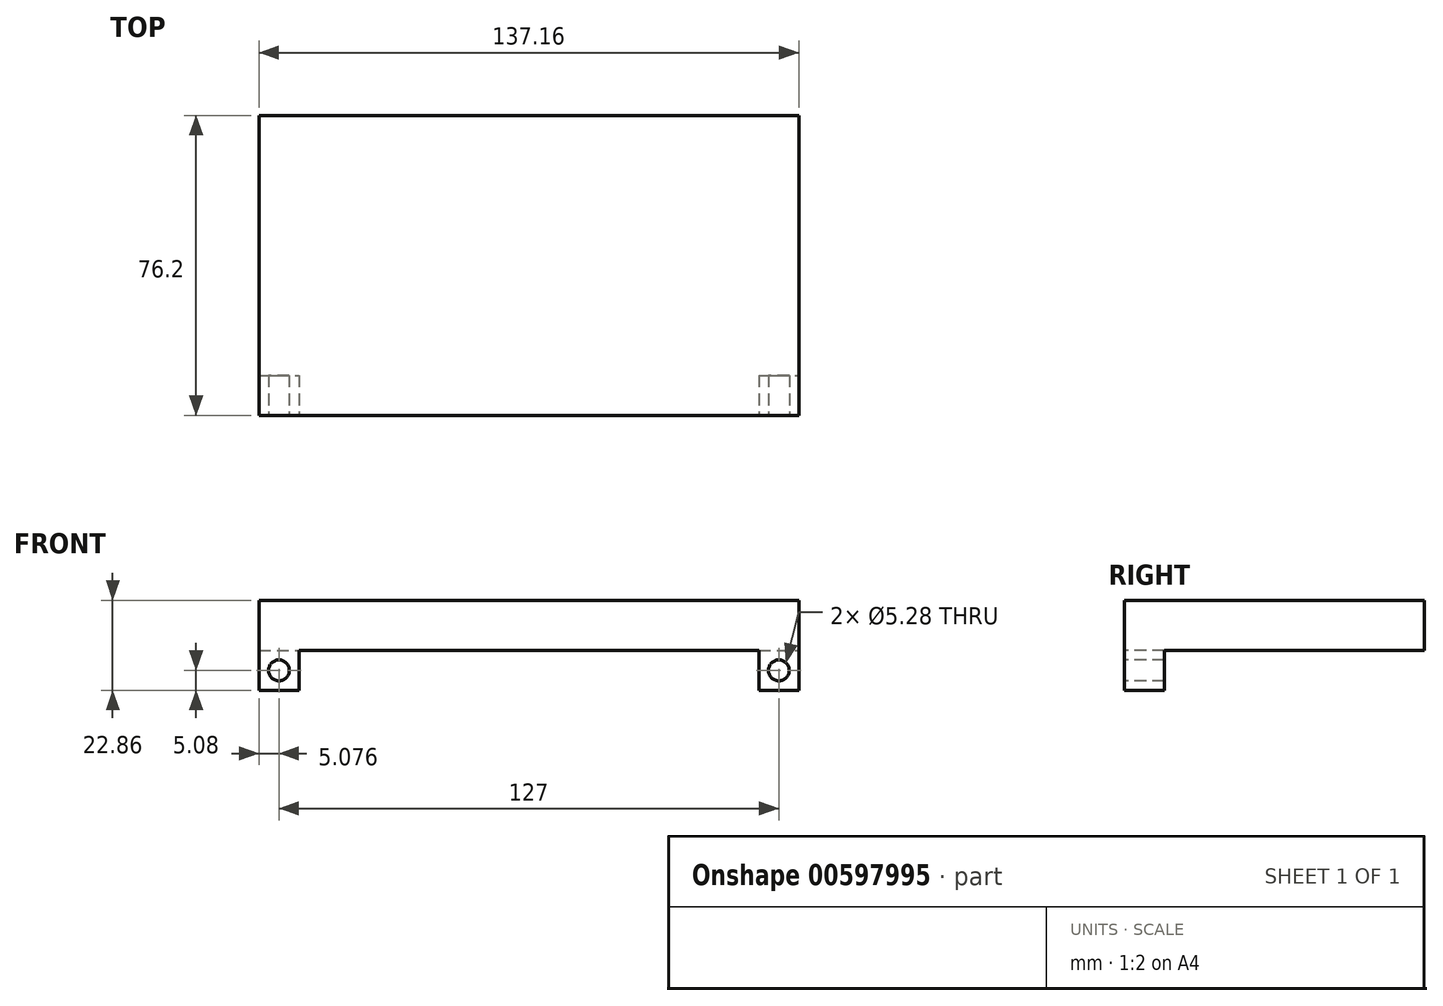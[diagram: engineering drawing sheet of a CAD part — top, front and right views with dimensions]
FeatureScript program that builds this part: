
annotation { "Feature Type Name" : "Feature", "Feature Type Description" : "" }
export const myFeature = defineFeature(function(context is Context, id is Id, definition is map)
    precondition{}
    {
        {
            var Q0;
            Q0=qCreatedBy(makeId("Front.planeOp"),FACE);
            var sketch = newSketch(context, id + "F0", { "sketchPlane" : qUnion([Q0])});
            skLineSegment(sketch, "E0.bottom", {"start": v(-68.27, 6.35) * mm, "end": v(68.89, 6.35) * mm});
            skLineSegment(sketch, "E0.top", {"start": v(-68.27, -6.35) * mm, "end": v(68.89, -6.35) * mm});
            skLineSegment(sketch, "E0.left", {"start": v(-68.27, 6.35) * mm, "end": v(-68.27, -6.35) * mm});
            skLineSegment(sketch, "E0.right", {"start": v(68.89, 6.35) * mm, "end": v(68.89, -6.35) * mm});
            skPoint(sketch, "E0.middle", {"position": v(0.3, 0) * mm});
            skSolve(sketch);
        }
        {
            var Q0;
            Q0=qSketchRegion(id+"F0",true);
            extrude(context, id + "F1", {"entities" : qUnion([Q0]), "depth" : 76.2 * mm, "offsetDistance" : 25.4 * mm});
        }
        {
            var Q0;
            Q0=makeQuery(id+"F1.opExtrude","CAP_FACE",FACE,{"disambiguationData":[OSD([sQuery(id+"F0.wireOp",EDGE,"E0.bottom"),sQuery(id+"F0.wireOp",EDGE,"E0.top"),sQuery(id+"F0.wireOp",EDGE,"E0.left"),sQuery(id+"F0.wireOp",EDGE,"E0.right")])],"isStart":false});
            var sketch = newSketch(context, id + "F2", { "sketchPlane" : qUnion([Q0])});
            skLineSegment(sketch, "E1", {"start": v(-68.27, -6.35) * mm, "end": v(-68.27, -16.5) * mm});
            skLineSegment(sketch, "E2", {"start": v(-68.27, -16.5) * mm, "end": v(-58.11, -16.5) * mm});
            skLineSegment(sketch, "E3", {"start": v(-58.11, -16.5) * mm, "end": v(-58.11, -6.35) * mm});
            skLineSegment(sketch, "E4", {"start": v(-58.11, -6.35) * mm, "end": v(-68.27, -6.35) * mm});
            skLineSegment(sketch, "E5.bottom", {"start": v(68.89, -6.35) * mm, "end": v(58.73, -6.35) * mm});
            skLineSegment(sketch, "E5.top", {"start": v(68.89, -16.51) * mm, "end": v(58.73, -16.51) * mm});
            skLineSegment(sketch, "E5.left", {"start": v(68.89, -6.35) * mm, "end": v(68.89, -16.51) * mm});
            skLineSegment(sketch, "E5.right", {"start": v(58.73, -6.35) * mm, "end": v(58.73, -16.51) * mm});
            skSolve(sketch);
        }
        {
            var Q0;
            Q0=qSketchRegion(id+"F2",true);
            extrude(context, id + "F3", {"entities" : qUnion([Q0]), "operationType" : NewBodyOperationType.ADD, "depth" : -10.16 * mm, "offsetDistance" : 25.4 * mm});
        }
        {
            var Q0;
            Q0=makeQuery(id+"F3.boolean.opBoolean","MERGE",FACE,{"derivedFrom":[makeQuery(id+"F1.opExtrude","CAP_FACE",FACE,{"disambiguationData":[OSD([sQuery(id+"F0.wireOp",EDGE,"E0.bottom"),sQuery(id+"F0.wireOp",EDGE,"E0.top"),sQuery(id+"F0.wireOp",EDGE,"E0.left"),sQuery(id+"F0.wireOp",EDGE,"E0.right")])],"isStart":false}),makeQuery(id+"F3.opExtrude","CAP_FACE",FACE,{"disambiguationData":[OSD([sQuery(id+"F2.wireOp",EDGE,"E1"),sQuery(id+"F2.wireOp",EDGE,"E2"),sQuery(id+"F2.wireOp",EDGE,"E3"),sQuery(id+"F2.wireOp",EDGE,"E4")])],"isStart":true}),makeQuery(id+"F3.opExtrude","CAP_FACE",FACE,{"disambiguationData":[OSD([sQuery(id+"F2.wireOp",EDGE,"E5.bottom"),sQuery(id+"F2.wireOp",EDGE,"E5.top"),sQuery(id+"F2.wireOp",EDGE,"E5.left"),sQuery(id+"F2.wireOp",EDGE,"E5.right")])],"isStart":true})]});
            var sketch = newSketch(context, id + "F4", { "sketchPlane" : qUnion([Q0])});
            skCircle(sketch, "E6", {"center": v(-63.2, -11.43) * mm, "radius": 2.64 * mm});
            skCircle(sketch, "E7", {"center": v(63.8, -11.43) * mm, "radius": 2.64 * mm});
            skSolve(sketch);
        }
        {
            var Q0;
            Q0=qSketchRegion(id+"F4",true);
            extrude(context, id + "F5", {"entities" : qUnion([Q0]), "operationType" : NewBodyOperationType.REMOVE, "oppositeDirection" : true, "depth" : 25.4 * mm, "offsetDistance" : 25.4 * mm});
        }
    });
